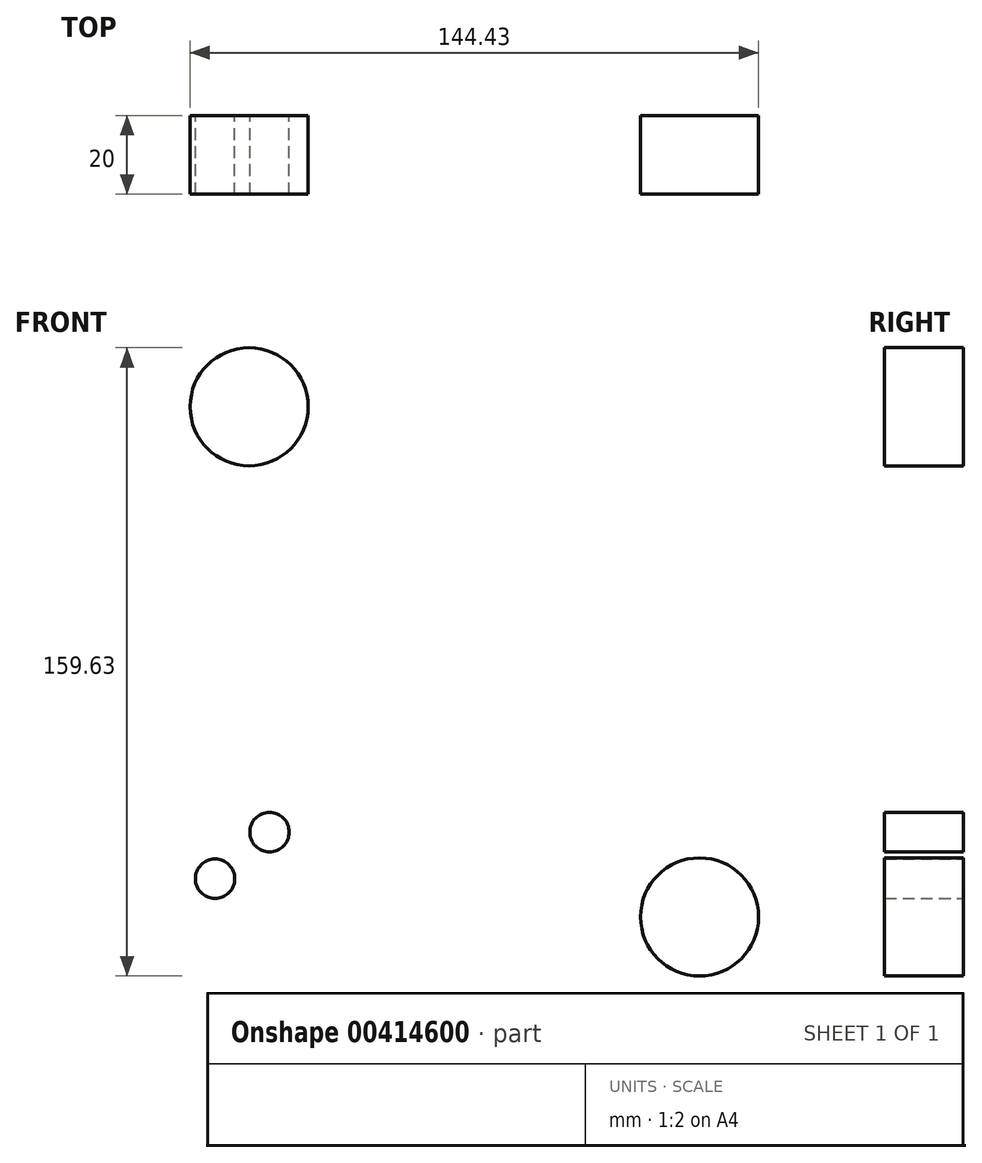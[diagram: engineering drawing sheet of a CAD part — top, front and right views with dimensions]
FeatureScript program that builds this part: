
annotation { "Feature Type Name" : "Feature", "Feature Type Description" : "" }
export const myFeature = defineFeature(function(context is Context, id is Id, definition is map)
    precondition{}
    {
        {
            var Q0;
            Q0=qCreatedBy(makeId("Front.planeOp"),FACE);
            var sketch = newSketch(context, id + "F0", { "sketchPlane" : qUnion([Q0])});
            skCircle(sketch, "E0", {"center": v(-64.4, 40.73) * mm, "radius": 15 * mm});
            skCircle(sketch, "E1", {"center": v(50.03, -88.9) * mm, "radius": 15 * mm});
            skCircle(sketch, "E2", {"center": v(-73.07, -79.18) * mm, "radius": 5 * mm});
            skCircle(sketch, "E3", {"center": v(-59.23, -67.35) * mm, "radius": 5 * mm});
            skSolve(sketch);
        }
        {
            var Q0;
            Q0=qSketchRegion(id+"F0",true);
            extrude(context, id + "F1", {"entities" : qUnion([Q0]), "endBound" : BoundingType.SYMMETRIC, "depth" : 20 * mm});
        }
    });
